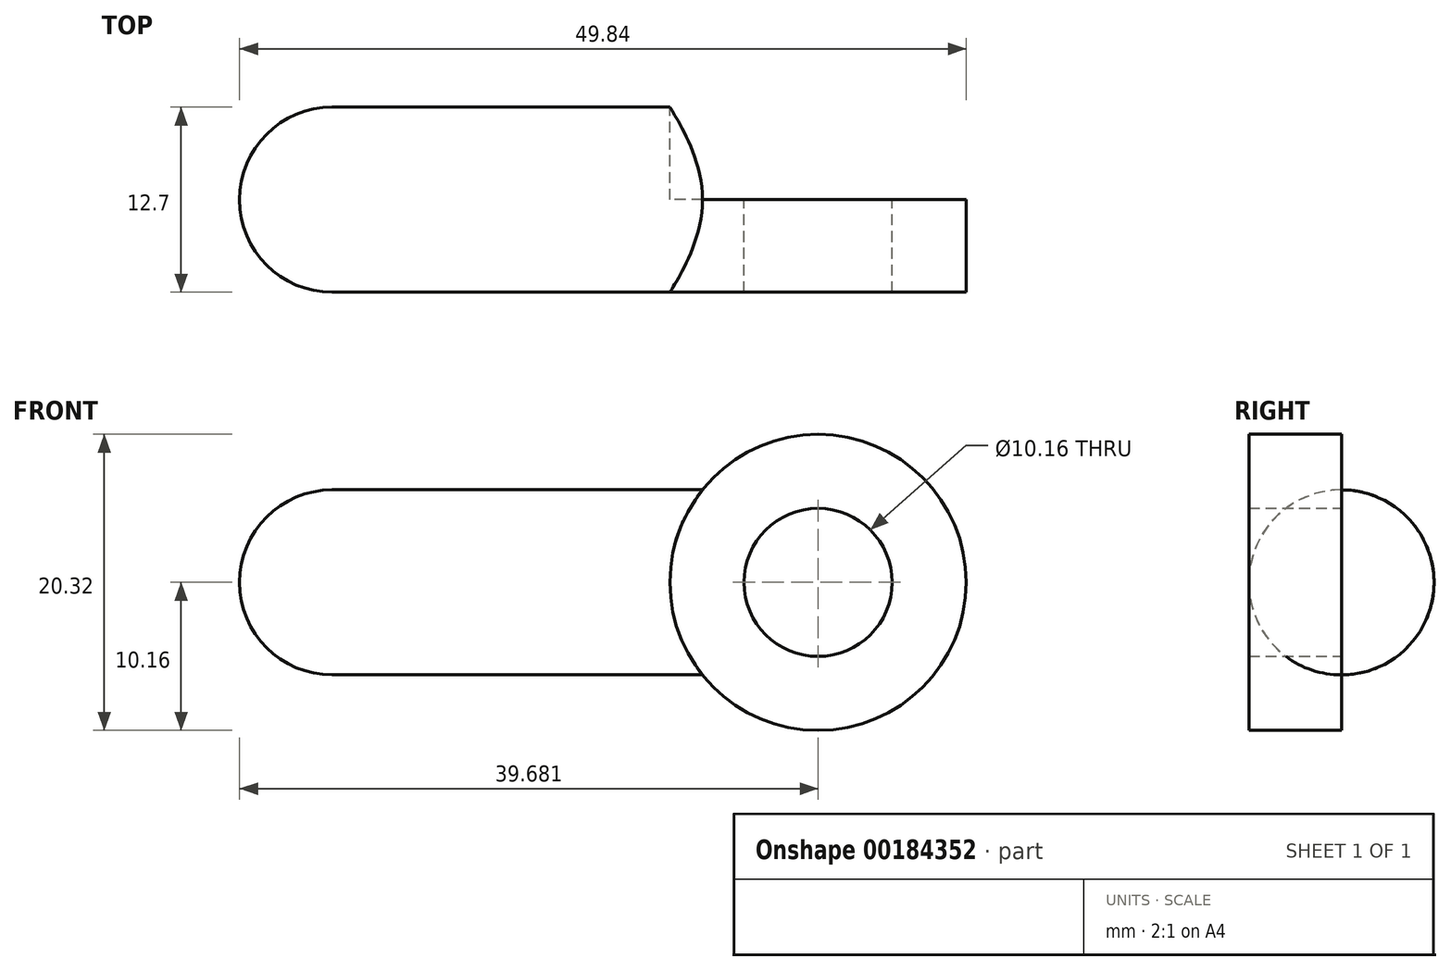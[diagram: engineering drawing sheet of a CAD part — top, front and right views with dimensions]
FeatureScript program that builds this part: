
annotation { "Feature Type Name" : "Feature", "Feature Type Description" : "" }
export const myFeature = defineFeature(function(context is Context, id is Id, definition is map)
    precondition{}
    {
        {
            var Q0;
            Q0=qCreatedBy(makeId("Front.planeOp"),FACE);
            var sketch = newSketch(context, id + "F0", { "sketchPlane" : qUnion([Q0])});
            skLineSegment(sketch, "E0.bottom", {"start": v(-12.7, 6.35) * mm, "end": v(12.7, 6.35) * mm});
            skLineSegment(sketch, "E0.top", {"start": v(-12.7, -6.35) * mm, "end": v(12.7, -6.35) * mm});
            skLineSegment(sketch, "E0.left", {"start": v(-12.7, 6.35) * mm, "end": v(-12.7, -6.35) * mm});
            skLineSegment(sketch, "E0.right", {"start": v(12.7, 6.35) * mm, "end": v(12.7, -6.35) * mm});
            skPoint(sketch, "E0.middle", {"position": v(0, 0) * mm});
            skCircle(sketch, "E1", {"center": v(20.63, 0) * mm, "radius": 10.16 * mm});
            skPoint(sketch, "E1.third.point", {"position": v(30.8, 0) * mm});
            skPoint(sketch, "E2.third.point.positionSnap0", {"position": v(-12.7, 0) * mm});
            skCircle(sketch, "E3", {"center": v(20.63, 0) * mm, "radius": 5.08 * mm});
            skArc(sketch, "E4", {"start": v(-12.7, 6.35) * mm, "mid": v(-19.05, 0) * mm, "end": v(-12.7, -6.35) * mm});
            skSolve(sketch);
        }
        {
            var Q0;
            {var subQ0=sQuery(id+"F0.wireOp",EDGE,"E0.bottom");Q0=makeQuery(id+"F0.imprint","IMPRINT",FACE,{"disambiguationData":[TD([[makeQuery(id+"F0.imprint","IMPRINT",EDGE,{"derivedFrom":subQ0}),-1.0]])]});}
            var Q1;
            Q1=makeQuery(id+"F0.imprint","IMPRINT",FACE,{"disambiguationData":[TD([[makeQuery(id+"F0.imprint","IMPRINT",EDGE,{"derivedFrom":sQuery(id+"F0.wireOp",EDGE,"E0.left")}),-1.0]])]});
            extrude(context, id + "F1", {"entities" : qUnion([Q0, Q1]), "endBound" : BoundingType.SYMMETRIC, "depth" : 12.7 * mm});
        }
        {
            var Q0;
            Q0=makeQuery(id+"F1.opExtrude","CAP_EDGE",EDGE,{"disambiguationData":[OSD([sQuery(id+"F0.wireOp",EDGE,"E0.bottom")])],"isStart":false});
            var Q1;
            Q1=makeQuery(id+"F1.opExtrude","CAP_EDGE",EDGE,{"disambiguationData":[OSD([sQuery(id+"F0.wireOp",EDGE,"E0.bottom")])],"isStart":true});
            var Q2;
            Q2=makeQuery(id+"F1.opExtrude","CAP_EDGE",EDGE,{"disambiguationData":[OSD([sQuery(id+"F0.wireOp",EDGE,"E0.top")])],"isStart":false});
            var Q3;
            Q3=makeQuery(id+"F1.opExtrude","CAP_EDGE",EDGE,{"disambiguationData":[OSD([sQuery(id+"F0.wireOp",EDGE,"E0.top")])],"isStart":true});
            fillet(context, id + "F2", {"entities" : qUnion([Q0, Q1, Q2, Q3]), "radius" : 6.35 * mm, "tangentPropagation" : true, "allowEdgeOverflow" : false});
        }
        {
            var Q0;
            {var subQ0=sQuery(id+"F0.wireOp",EDGE,"E0.right");Q0=makeQuery(id+"F0.imprint","IMPRINT",FACE,{"disambiguationData":[TD([[makeQuery(id+"F0.imprint","IMPRINT",EDGE,{"derivedFrom":subQ0}),1.0]])]});}
            var Q1;
            {var subQ0=sQuery(id+"F0.wireOp",EDGE,"E0.right");Q1=makeQuery(id+"F0.imprint","IMPRINT",FACE,{"disambiguationData":[TD([[makeQuery(id+"F0.imprint","IMPRINT",EDGE,{"derivedFrom":subQ0}),-1.0]])]});}
            extrude(context, id + "F3", {"entities" : qUnion([Q0, Q1]), "operationType" : NewBodyOperationType.ADD, "depth" : 6.35 * mm});
        }
    });
